# Revit family: PRD_FrankeWS_WlHngWshBsns_ANIMASingleWashbasin_ANMX460_ANMX461
name_source: partatom
category: Plumbing Fixtures
revit_build: Autodesk Revit 2018 (Build: 20190510_1515(x64)
units: mm (PartAtom-declared; Revit-internal decimal feet)

## family parameters
Cut with Voids When Loaded = Yes
Host = Face
OmniClass Number = 23.45.05.14.14.27
OmniClass Title = Service Sinks
Part Type = Normal
Room Calculation Point = No
Round Connector Dimension = Use Diameter
Shared = Yes

## types (2) — shared parameters
AssetType = Fixed
BowlDepth = 360.00 mm
BowlFinish = Satin finish
BowlHeight = 140.00 mm
BowlPosition = Center
BowlShape = Circle with straight sides
BowlWidth = 420.00 mm
Category = Pr_40_20_96_96, Wall-hung washbasins
Default Elevation = 925 mm  [stored 3.03478 ft]
DiameterNominal = 50  [stored 0.164042 ft]
DrainSize = 50 mm  [stored 0.164042 ft]
DurationUnit = year
Features = stainless steel, surface satin finished, material thickness 1.2 mm
Finish = Satin finish
Flow = 0.0 L/s
IfcExportAs = IfcSanitaryTerminalType
IfcExportType = WASHHANDBASIN
IntegralAccessories = fixing material included
Manufacturer = KWC Group AG
ManufacturerName = KWC Group AG
ManufacturerURL = www.kwc.com
Material = stainless steel
MaterialCode = 1.4301 Chrome Nickel steel V2A
MaterialThickness = 1.20 mm
Mounting = WallHung
NBSDescription = Wall hung wash basins
NBSReference = 45-35-70/369
NominalDepth = 490 mm  [stored 1.60761 ft]
NominalHeight = 170 mm  [stored 0.557743 ft]
NominalWidth = 460 mm  [stored 1.50919 ft]
NumberOfBowls = 1
ProductInformation = https://pim.kwc.com
RearUpstand = No
SinkMaterial = PRD_AR_StainlessSteel_SatinFinished
SiphonDiameter = DN 50
SiphonIncluded = Yes
Size = 460 x 170 x 490 mm (W x H x D)
Splashback = No
TapLedge = Yes
TypeOfBasin = Wash basin
TypeOfMounting = Wall mounting
TypeOfWasteKit = Welded perforated waste (non removable)
URL = www.kwc.com
Uniclass2015Code = Pr_40_20_96_96
Uniclass2015Title = Wall-hung washbasins
Uniclass2015Version = Products v1.23
Version = 1
WarrantyDurationUnit = year
WashHandBasinType = HandRinse
WasteHolePosition = Center back
WasteHoleProjection = 215.00 mm
WasteKitIncluded = Yes
WasteSize = DN 32
zero-valued in all types: MountingOffset

## per-type parameters (varying)
| type | BIMObjectName | Description | GrossWeight | ModelNumber | Name | NetWeight | NumberOfTapHoles | Overflow | ProductCode | Spillway | TailorMade | TapHole | TapHoleDiameter | TapHolePosition |
| ANMX460 | PRD_AR_WallHungWashbasins_ANIMASingleWashbasin_ANMX460 | Single wash basin for wall-mounting, made of stainless steel, surface satin finished, material thickness 1.2 mm. Seamless wash basin in one piece with rounded edges, tap landing without tap hole, strainer waste valve, DN 40/50 siphon included, without overflow. Mounting from the front, fixing material included. Wash basin suitable for areas exposed to vandalism and wheelchair users. | 9.10 kg | 2000102710 | ANIMA Single washbasin ANMX460 | 9.00 kg | 0 |  | 203.0521.091 |  |  | No |  |  |
| ANMX461 | PRD_AR_WallHungWashbasins_ANIMASingleWashbasin_ANMX461 | Single wash basin for wall-mounting, made of stainless steel, surface satin finished, material thickness 1.2 mm. Seamless wash basin in one piece with rounded edges, tap landing with tap hole 35 mm, strainer waste valve, DN 40/50 siphon included, without overflow. Mounting from the front, fixing material included. Wash basin suitable for areas exposed to vandalism and wheelchair users. | 9.26 kg | 2000102711 | ANIMA Single washbasin ANMX461 | 8.80 kg | 1 | No | 203.0637.183 | No | No | Yes | 35.00 mm | Middle |

note: column(s) folded — value = type name in every type: Model, ModelReference

note: [stored X ft] marks values corroborated as IEEE doubles in the binary element streams (Revit-internal decimal feet)

## geometry (parser evidence)
native form markers: Sweep x5
no freeform markers — native parametric forms only
